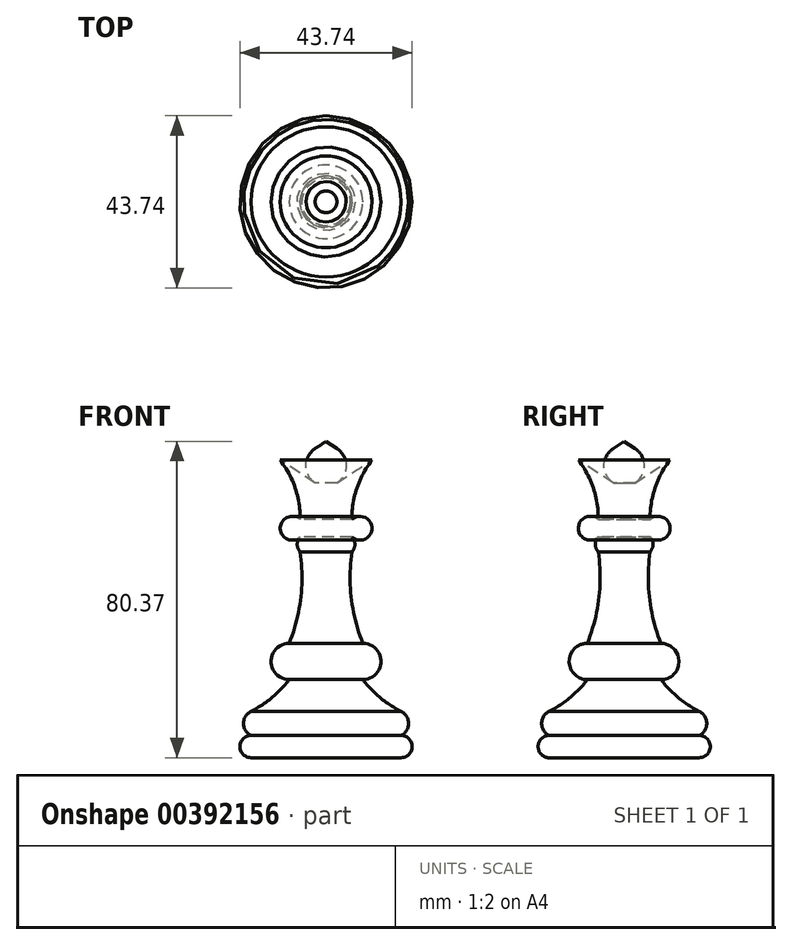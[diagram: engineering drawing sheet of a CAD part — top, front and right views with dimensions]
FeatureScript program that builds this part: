
annotation { "Feature Type Name" : "Feature", "Feature Type Description" : "" }
export const myFeature = defineFeature(function(context is Context, id is Id, definition is map)
    precondition{}
    {
        {
            var Q0;
            Q0=qCreatedBy(makeId("Front.planeOp"),FACE);
            var sketch = newSketch(context, id + "F0", { "sketchPlane" : qUnion([Q0])});
            skLineSegment(sketch, "E0", {"start": v(0, 35.49) * mm, "end": v(0, -34.36) * mm});
            skLineSegment(sketch, "E1", {"start": v(0, -34.36) * mm, "end": v(-19.05, -34.36) * mm});
            skArc(sketch, "E2", {"start": v(-19.05, -28.71) * mm, "mid": v(-21.87, -31.54) * mm, "end": v(-19.05, -34.36) * mm});
            skArc(sketch, "E3", {"start": v(-19.05, -22.58) * mm, "mid": v(-20.97, -25.65) * mm, "end": v(-19.05, -28.71) * mm});
            skArc(sketch, "E4", {"start": v(-19.05, -22.58) * mm, "mid": v(-13.76, -19.09) * mm, "end": v(-9.36, -14.52) * mm});
            skArc(sketch, "E5", {"start": v(-9.36, -5.3) * mm, "mid": v(-13.97, -9.9) * mm, "end": v(-9.36, -14.52) * mm});
            skArc(sketch, "E6", {"start": v(-9.36, -5.3) * mm, "mid": v(-6.43, 6.14) * mm, "end": v(-6.58, 17.94) * mm});
            skArc(sketch, "E7", {"start": v(-6.58, 21.74) * mm, "mid": v(-7.34, 19.84) * mm, "end": v(-6.58, 17.94) * mm});
            skLineSegment(sketch, "E8", {"start": v(0, 40.97) * mm, "end": v(0, 35.49) * mm});
            skPoint(sketch, "E9", {"position": v(-2.77, 35.49) * mm});
            skArc(sketch, "E10", {"start": v(-6.58, 26.13) * mm, "mid": v(-11.67, 23.94) * mm, "end": v(-6.58, 21.74) * mm});
            skArc(sketch, "E11", {"start": v(-6.58, 26.13) * mm, "mid": v(-7.82, 34.15) * mm, "end": v(-11.67, 41.3) * mm});
            skPoint(sketch, "E11.endSnap0", {"position": v(-11.67, 23.94) * mm});
            skLineSegment(sketch, "E12", {"start": v(-11.67, 41.3) * mm, "end": v(-2.77, 35.49) * mm});
            skArc(sketch, "E13", {"start": v(-2.77, 44.2) * mm, "mid": v(-5.13, 39.84) * mm, "end": v(-2.77, 35.49) * mm});
            skLineSegment(sketch, "E14", {"start": v(-2.77, 44.2) * mm, "end": v(0, 46) * mm});
            skLineSegment(sketch, "E15", {"start": v(0, 35.49) * mm, "end": v(0, 46) * mm});
            skSolve(sketch);
        }
        {
            var Q0;
            Q0 = qSketchRegion(id + "F0", true);
            var Q1;
            Q1=sQuery(id+"F0.wireOp",EDGE,"E0");
            revolve(context, id + "F1", {"entities" : qUnion([Q0]), "axis" : qUnion([Q1]), "revolveType" : RevolveType.FULL});
        }
    });
